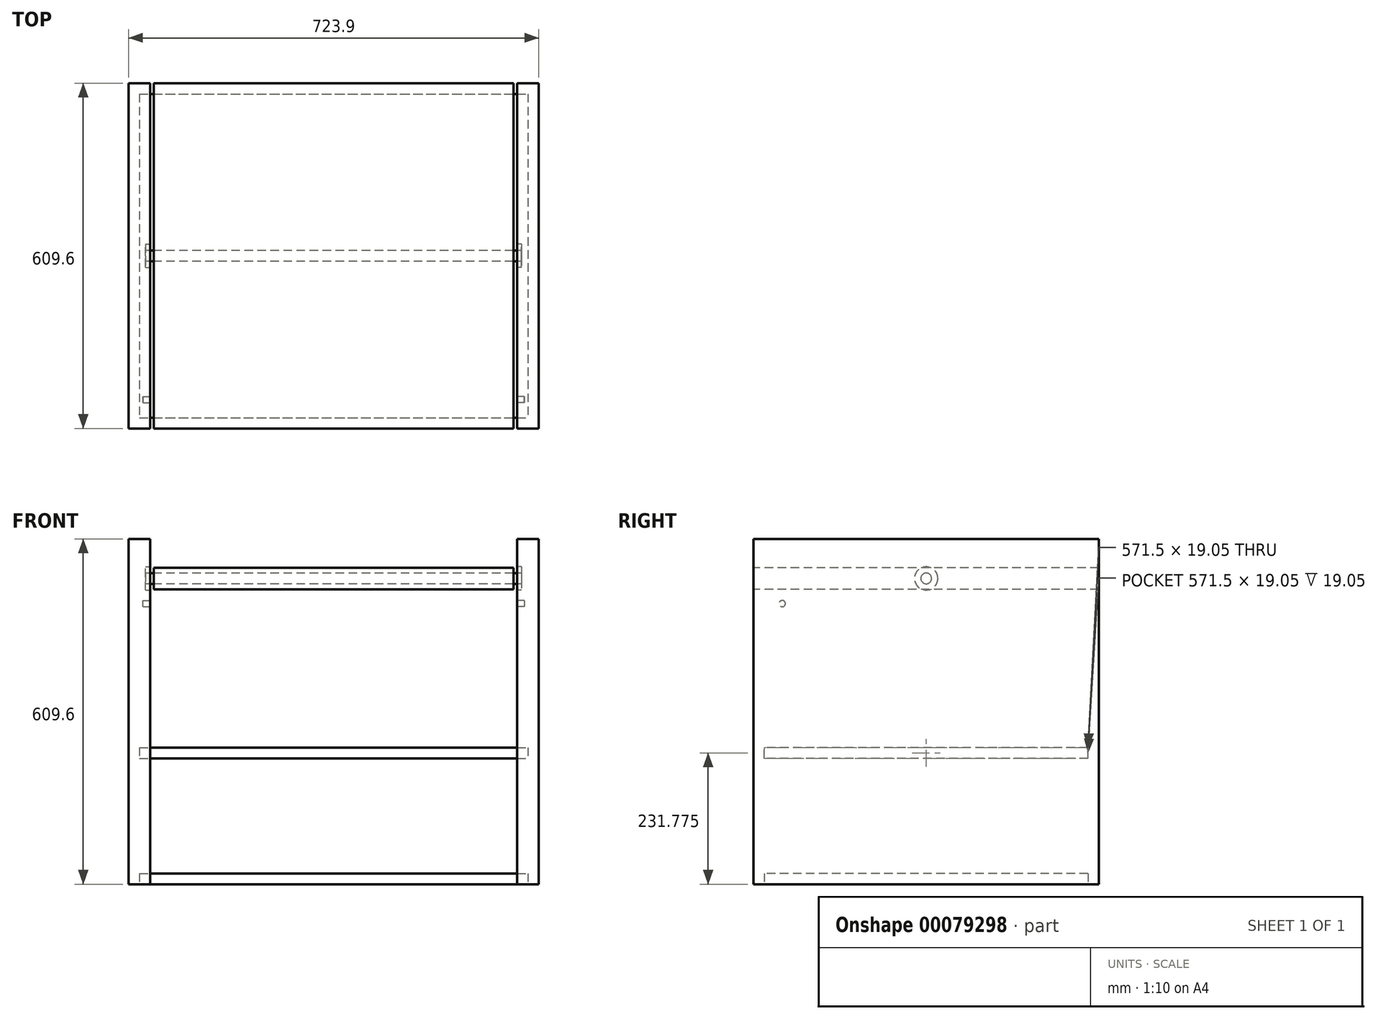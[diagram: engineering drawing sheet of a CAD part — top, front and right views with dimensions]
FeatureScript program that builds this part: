
annotation { "Feature Type Name" : "Feature", "Feature Type Description" : "" }
export const myFeature = defineFeature(function(context is Context, id is Id, definition is map)
    precondition{}
    {
        {
            var Q0;
            Q0=qCreatedBy(makeId("Front.planeOp"),FACE);
            var sketch = newSketch(context, id + "F0", { "sketchPlane" : qUnion([Q0])});
            skLineSegment(sketch, "E0.bottom", {"start": v(0, 0) * mm, "end": v(38.1, 0) * mm});
            skLineSegment(sketch, "E0.top", {"start": v(0, 609.6) * mm, "end": v(38.1, 609.6) * mm});
            skLineSegment(sketch, "E0.left", {"start": v(0, 0) * mm, "end": v(0, 609.6) * mm});
            skLineSegment(sketch, "E0.right", {"start": v(38.1, 0) * mm, "end": v(38.1, 609.6) * mm});
            skSolve(sketch);
        }
        {
            var Q0;
            Q0 = qSketchRegion(id + "F0", true);
            extrude(context, id + "F1", {"entities" : qUnion([Q0]), "depth" : 609.6 * mm});
        }
        {
            var Q0;
            Q0=makeQuery(id+"F1.opExtrude","SWEPT_BODY",BODY,{"disambiguationData":[OSD([sQuery(id+"F0.wireOp",EDGE,"E0.bottom"),sQuery(id+"F0.wireOp",EDGE,"E0.top"),sQuery(id+"F0.wireOp",EDGE,"E0.left"),sQuery(id+"F0.wireOp",EDGE,"E0.right")])]});
            transform(context, id + "F2", {"entities" : qUnion([Q0]), "transformType" : TransformType.TRANSLATION_3D, "dx" : 685.8 * mm, "dy" : 0 * mm, "dz" : 0 * mm, "makeCopy" : true});
        }
        {
            var Q0;
            Q0=makeQuery(id+"F1.opExtrude","CAP_FACE",FACE,{"disambiguationData":[OSD([sQuery(id+"F0.wireOp",EDGE,"E0.bottom"),sQuery(id+"F0.wireOp",EDGE,"E0.top"),sQuery(id+"F0.wireOp",EDGE,"E0.left"),sQuery(id+"F0.wireOp",EDGE,"E0.right")])],"isStart":false});
            cPlane(context, id + "F3", {"entities" : qUnion([Q0]), "cplaneType" : CPlaneType.OFFSET, "offset" : 19.05 * mm, "oppositeDirection" : true, "width" : 152.4 * mm, "height" : 152.4 * mm});
        }
        {
            var Q0;
            Q0=qCreatedBy(id+"F3.planeOp",FACE);
            var sketch = newSketch(context, id + "F4", { "sketchPlane" : qUnion([Q0])});
            skLineSegment(sketch, "E1.bottom", {"start": v(19.05, 19.05) * mm, "end": v(704.85, 19.05) * mm});
            skLineSegment(sketch, "E1.top", {"start": v(19.05, 0) * mm, "end": v(704.85, 0) * mm});
            skLineSegment(sketch, "E1.left", {"start": v(19.05, 19.05) * mm, "end": v(19.05, 0) * mm});
            skLineSegment(sketch, "E1.right", {"start": v(704.85, 19.05) * mm, "end": v(704.85, 0) * mm});
            skSolve(sketch);
        }
        {
            var Q0;
            Q0 = qSketchRegion(id + "F4", true);
            extrude(context, id + "F5", {"entities" : qUnion([Q0]), "oppositeDirection" : true, "depth" : 571.5 * mm});
        }
        {
            var Q0;
            Q0=makeQuery(id+"F5.opExtrude","SWEPT_BODY",BODY,{"disambiguationData":[OSD([sQuery(id+"F4.wireOp",EDGE,"E1.bottom"),sQuery(id+"F4.wireOp",EDGE,"E1.top"),sQuery(id+"F4.wireOp",EDGE,"E1.left"),sQuery(id+"F4.wireOp",EDGE,"E1.right")])]});
            var Q1;
            Q1=makeQuery(id+"F1.opExtrude","SWEPT_BODY",BODY,{"disambiguationData":[OSD([sQuery(id+"F0.wireOp",EDGE,"E0.bottom"),sQuery(id+"F0.wireOp",EDGE,"E0.top"),sQuery(id+"F0.wireOp",EDGE,"E0.left"),sQuery(id+"F0.wireOp",EDGE,"E0.right")])]});
            var Q2;
            Q2=makeQuery(id+"F2.opPattern","COPY",BODY,{"derivedFrom":makeQuery(id+"F1.opExtrude","SWEPT_BODY",BODY,{"disambiguationData":[OSD([sQuery(id+"F0.wireOp",EDGE,"E0.bottom"),sQuery(id+"F0.wireOp",EDGE,"E0.top"),sQuery(id+"F0.wireOp",EDGE,"E0.left"),sQuery(id+"F0.wireOp",EDGE,"E0.right")])]}),"instanceName":"1"});
            booleanBodies(context, id + "F6", {"operationType" : BooleanOperationType.SUBTRACTION, "tools" : qUnion([Q0]), "targets" : qUnion([Q1, Q2]), "keepTools" : true});
        }
        {
            var Q0;
            Q0=qCreatedBy(id+"F3.planeOp",FACE);
            var sketch = newSketch(context, id + "F7", { "sketchPlane" : qUnion([Q0])});
            skLineSegment(sketch, "E2.bottom", {"start": v(19.05, 241.3) * mm, "end": v(704.85, 241.3) * mm});
            skLineSegment(sketch, "E2.top", {"start": v(19.05, 222.25) * mm, "end": v(704.85, 222.25) * mm});
            skLineSegment(sketch, "E2.left", {"start": v(19.05, 241.3) * mm, "end": v(19.05, 222.25) * mm});
            skLineSegment(sketch, "E2.right", {"start": v(704.85, 241.3) * mm, "end": v(704.85, 222.25) * mm});
            skSolve(sketch);
        }
        {
            var Q0;
            Q0 = qSketchRegion(id + "F7", true);
            extrude(context, id + "F8", {"entities" : qUnion([Q0]), "oppositeDirection" : true, "depth" : 571.5 * mm});
        }
        {
            var Q0;
            Q0=makeQuery(id+"F8.opExtrude","SWEPT_BODY",BODY,{"disambiguationData":[OSD([sQuery(id+"F7.wireOp",EDGE,"E2.bottom"),sQuery(id+"F7.wireOp",EDGE,"E2.top"),sQuery(id+"F7.wireOp",EDGE,"E2.left"),sQuery(id+"F7.wireOp",EDGE,"E2.right")])]});
            var Q1;
            Q1=makeQuery(id+"F1.opExtrude","SWEPT_BODY",BODY,{"disambiguationData":[OSD([sQuery(id+"F0.wireOp",EDGE,"E0.bottom"),sQuery(id+"F0.wireOp",EDGE,"E0.top"),sQuery(id+"F0.wireOp",EDGE,"E0.left"),sQuery(id+"F0.wireOp",EDGE,"E0.right")])]});
            var Q2;
            Q2=makeQuery(id+"F2.opPattern","COPY",BODY,{"derivedFrom":makeQuery(id+"F1.opExtrude","SWEPT_BODY",BODY,{"disambiguationData":[OSD([sQuery(id+"F0.wireOp",EDGE,"E0.bottom"),sQuery(id+"F0.wireOp",EDGE,"E0.top"),sQuery(id+"F0.wireOp",EDGE,"E0.left"),sQuery(id+"F0.wireOp",EDGE,"E0.right")])]}),"instanceName":"1"});
            booleanBodies(context, id + "F9", {"operationType" : BooleanOperationType.SUBTRACTION, "tools" : qUnion([Q0]), "targets" : qUnion([Q1, Q2]), "keepTools" : true});
        }
        {
            var Q0;
            Q0=makeQuery(id+"F1.opExtrude","SWEPT_FACE",FACE,{"disambiguationData":[OSD([sQuery(id+"F0.wireOp",EDGE,"E0.right")])]});
            var sketch = newSketch(context, id + "F10", { "sketchPlane" : qUnion([Q0])});
            skCircle(sketch, "E3", {"center": v(-304.8, 539.75) * mm, "radius": 20.64 * mm});
            skPoint(sketch, "E3.centerSnap0", {"position": v(-304.8, 609.6) * mm});
            skSolve(sketch);
        }
        {
            var Q0;
            Q0 = qSketchRegion(id + "F10", true);
            extrude(context, id + "F11", {"entities" : qUnion([Q0]), "operationType" : NewBodyOperationType.REMOVE, "oppositeDirection" : true, "depth" : 7.94 * mm});
        }
        {
            var Q0;
            Q0=makeQuery(id+"F2.opPattern","COPY",FACE,{"derivedFrom":makeQuery(id+"F1.opExtrude","SWEPT_FACE",FACE,{"disambiguationData":[OSD([sQuery(id+"F0.wireOp",EDGE,"E0.left")])]}),"instanceName":"1"});
            var sketch = newSketch(context, id + "F12", { "sketchPlane" : qUnion([Q0])});
            skCircle(sketch, "E4", {"center": v(304.8, 539.75) * mm, "radius": 20.64 * mm});
            skPoint(sketch, "E4.centerSnap0", {"position": v(304.8, 609.6) * mm});
            skSolve(sketch);
        }
        {
            var Q0;
            Q0 = qSketchRegion(id + "F12", true);
            extrude(context, id + "F13", {"entities" : qUnion([Q0]), "operationType" : NewBodyOperationType.REMOVE, "oppositeDirection" : true, "depth" : 7.94 * mm});
        }
        {
            var Q0;
            Q0=makeQuery(id+"F11.boolean.opBoolean","COPY",FACE,{"derivedFrom":makeQuery(id+"F11.opExtrude","CAP_FACE",FACE,{"disambiguationData":[OSD([sQuery(id+"F10.wireOp",EDGE,"E3")])],"isStart":false})});
            var sketch = newSketch(context, id + "F14", { "sketchPlane" : qUnion([Q0])});
            skCircle(sketch, "E5", {"center": v(-304.8, 539.75) * mm, "radius": 9.53 * mm});
            skSolve(sketch);
        }
        {
            var Q0;
            Q0 = qSketchRegion(id + "F14", true);
            extrude(context, id + "F15", {"entities" : qUnion([Q0]), "endBound" : BoundingType.UP_TO_NEXT, "depth" : 25.4 * mm});
        }
        {
            var Q0;
            Q0=makeQuery(id+"F1.opExtrude","CAP_FACE",FACE,{"disambiguationData":[OSD([sQuery(id+"F0.wireOp",EDGE,"E0.bottom"),sQuery(id+"F0.wireOp",EDGE,"E0.top"),sQuery(id+"F0.wireOp",EDGE,"E0.left"),sQuery(id+"F0.wireOp",EDGE,"E0.right")])],"isStart":false});
            var sketch = newSketch(context, id + "F16", { "sketchPlane" : qUnion([Q0])});
            skLineSegment(sketch, "E6.bottom", {"start": v(44.45, 558.8) * mm, "end": v(679.45, 558.8) * mm});
            skLineSegment(sketch, "E6.top", {"start": v(44.45, 520.7) * mm, "end": v(679.45, 520.7) * mm});
            skLineSegment(sketch, "E6.left", {"start": v(44.45, 558.8) * mm, "end": v(44.45, 520.7) * mm});
            skLineSegment(sketch, "E6.right", {"start": v(679.45, 558.8) * mm, "end": v(679.45, 520.7) * mm});
            skSolve(sketch);
        }
        {
            var Q0;
            Q0 = qSketchRegion(id + "F16", true);
            extrude(context, id + "F17", {"entities" : qUnion([Q0]), "oppositeDirection" : true, "depth" : 609.6 * mm});
        }
        {
            var Q0;
            Q0=makeQuery(id+"F15.opExtrude","SWEPT_BODY",BODY,{"disambiguationData":[OSD([sQuery(id+"F14.wireOp",EDGE,"E5")])]});
            var Q1;
            Q1=makeQuery(id+"F17.opExtrude","SWEPT_BODY",BODY,{"disambiguationData":[OSD([sQuery(id+"F16.wireOp",EDGE,"E6.bottom"),sQuery(id+"F16.wireOp",EDGE,"E6.top"),sQuery(id+"F16.wireOp",EDGE,"E6.left"),sQuery(id+"F16.wireOp",EDGE,"E6.right")])]});
            booleanBodies(context, id + "F18", {"operationType" : BooleanOperationType.SUBTRACTION, "tools" : qUnion([Q0]), "targets" : qUnion([Q1]), "keepTools" : true});
        }
        {
            var Q0;
            Q0=makeQuery(id+"F1.opExtrude","SWEPT_FACE",FACE,{"disambiguationData":[OSD([sQuery(id+"F0.wireOp",EDGE,"E0.right")])]});
            var sketch = newSketch(context, id + "F19", { "sketchPlane" : qUnion([Q0])});
            skCircle(sketch, "E7", {"center": v(-558.8, 495.3) * mm, "radius": 5.56 * mm});
            skSolve(sketch);
        }
        {
            var Q0;
            Q0 = qSketchRegion(id + "F19", true);
            extrude(context, id + "F20", {"entities" : qUnion([Q0]), "operationType" : NewBodyOperationType.REMOVE, "oppositeDirection" : true, "depth" : 12.7 * mm});
        }
        {
            var Q0;
            Q0=makeQuery(id+"F2.opPattern","COPY",FACE,{"derivedFrom":makeQuery(id+"F1.opExtrude","SWEPT_FACE",FACE,{"disambiguationData":[OSD([sQuery(id+"F0.wireOp",EDGE,"E0.left")])]}),"instanceName":"1"});
            var sketch = newSketch(context, id + "F21", { "sketchPlane" : qUnion([Q0])});
            skCircle(sketch, "E8", {"center": v(558.8, 495.3) * mm, "radius": 5.56 * mm});
            skSolve(sketch);
        }
        {
            var Q0;
            Q0 = qSketchRegion(id + "F21", true);
            extrude(context, id + "F22", {"entities" : qUnion([Q0]), "operationType" : NewBodyOperationType.REMOVE, "oppositeDirection" : true, "depth" : 12.7 * mm});
        }
    });
